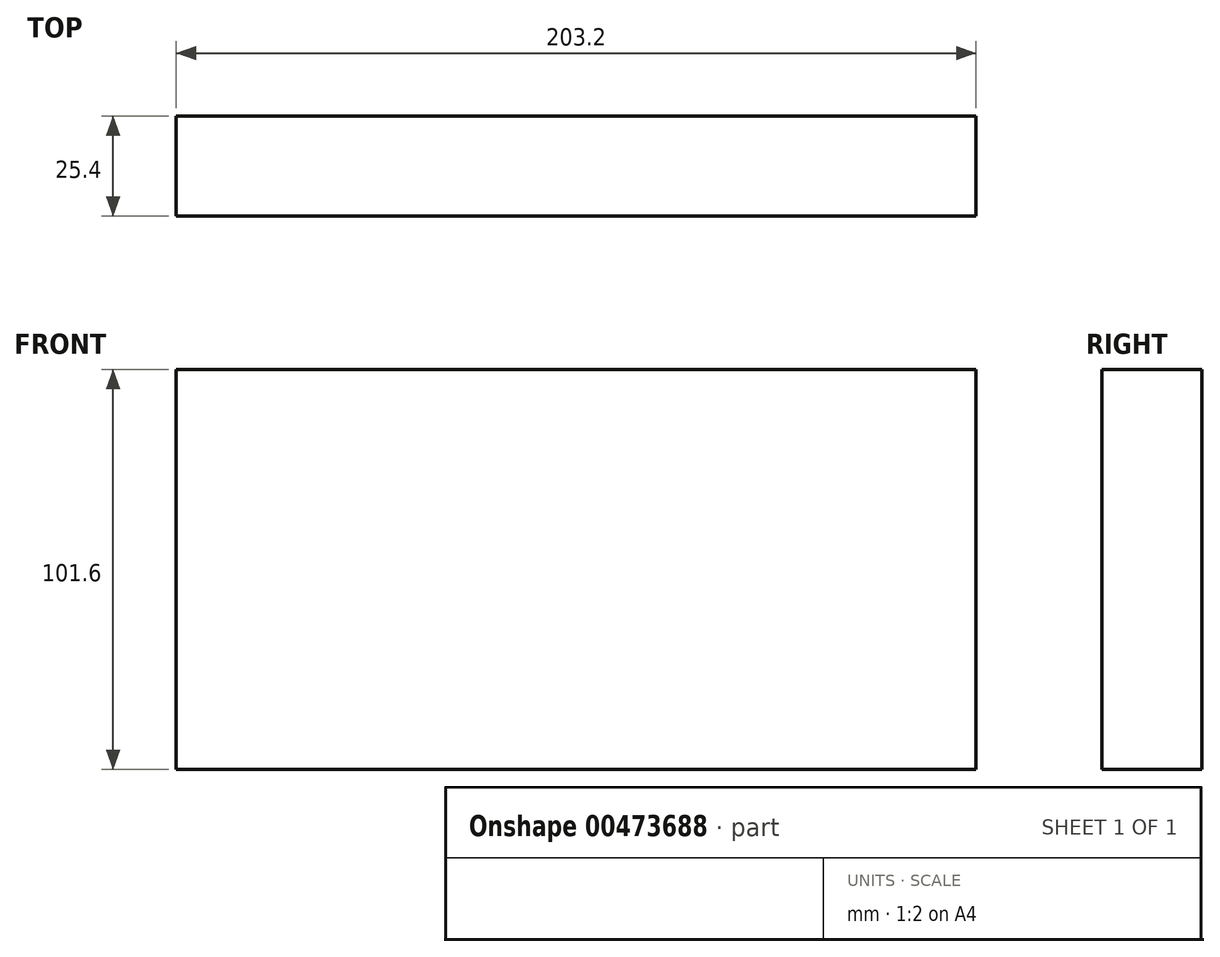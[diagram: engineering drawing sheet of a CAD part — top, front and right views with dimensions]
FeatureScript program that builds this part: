
annotation { "Feature Type Name" : "Feature", "Feature Type Description" : "" }
export const myFeature = defineFeature(function(context is Context, id is Id, definition is map)
    precondition{}
    {
        {
            var Q0;
            Q0=qCreatedBy(makeId("Front.planeOp"),FACE);
            var sketch = newSketch(context, id + "F0", { "sketchPlane" : qUnion([Q0])});
            skLineSegment(sketch, "E0.bottom", {"start": v(0, 0) * mm, "end": v(203.2, 0) * mm});
            skLineSegment(sketch, "E0.top", {"start": v(0, 101.6) * mm, "end": v(203.2, 101.6) * mm});
            skLineSegment(sketch, "E0.left", {"start": v(0, 0) * mm, "end": v(0, 101.6) * mm});
            skLineSegment(sketch, "E0.right", {"start": v(203.2, 0) * mm, "end": v(203.2, 101.6) * mm});
            skSolve(sketch);
        }
        {
            var Q0;
            Q0=qSketchRegion(id+"F0",true);
            extrude(context, id + "F1", {"entities" : qUnion([Q0]), "depth" : 25.4 * mm});
        }
    });
